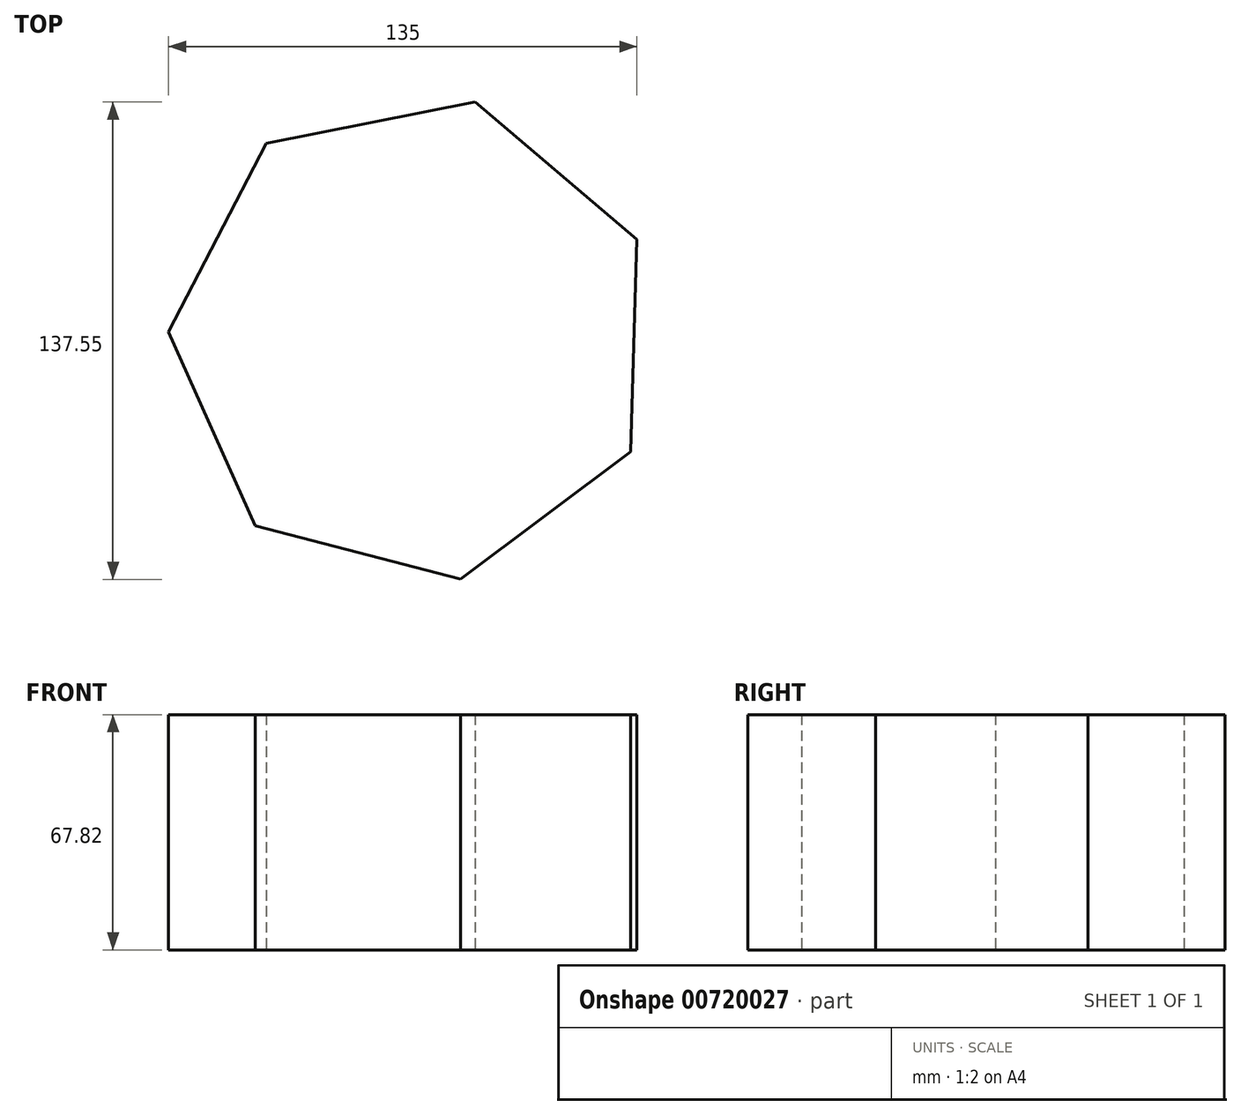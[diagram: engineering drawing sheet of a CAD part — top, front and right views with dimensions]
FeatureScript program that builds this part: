
annotation { "Feature Type Name" : "Feature", "Feature Type Description" : "" }
export const myFeature = defineFeature(function(context is Context, id is Id, definition is map)
    precondition{}
    {
        {
            var Q0;
            Q0=qCreatedBy(makeId("Top.planeOp"),FACE);
            var sketch = newSketch(context, id + "F0", { "sketchPlane" : qUnion([Q0])});
            skCircle(sketch, "E0.cCircle", {"center": v(0, 0) * mm, "radius": 63.58 * mm, "construction": true});
            skLineSegment(sketch, "E0.0", {"start": v(62.65, -32.5) * mm, "end": v(13.65, -69.24) * mm});
            skLineSegment(sketch, "E0.1", {"start": v(13.65, -69.24) * mm, "end": v(-45.62, -53.84) * mm});
            skLineSegment(sketch, "E0.2", {"start": v(-45.62, -53.84) * mm, "end": v(-70.54, 2.1) * mm});
            skLineSegment(sketch, "E0.3", {"start": v(-70.54, 2.1) * mm, "end": v(-42.34, 56.46) * mm});
            skLineSegment(sketch, "E0.4", {"start": v(-42.34, 56.46) * mm, "end": v(17.74, 68.3) * mm});
            skLineSegment(sketch, "E0.5", {"start": v(17.74, 68.3) * mm, "end": v(64.46, 28.72) * mm});
            skLineSegment(sketch, "E0.6", {"start": v(64.46, 28.72) * mm, "end": v(62.65, -32.5) * mm});
            skPoint(sketch, "E0.0.midPoint", {"position": v(38.15, -50.87) * mm});
            skSolve(sketch);
        }
        {
            var Q0;
            Q0=makeQuery(id+"F0.imprint","IMPRINT",FACE,{"disambiguationData":[TD([[makeQuery(id+"F0.imprint","IMPRINT",EDGE,{"derivedFrom":sQuery(id+"F0.wireOp",EDGE,"E0.0")}),-1.0]])]});
            extrude(context, id + "F1", {"entities" : qUnion([Q0]), "depth" : 67.82 * mm, "offsetDistance" : 25.4 * mm});
        }
    });
